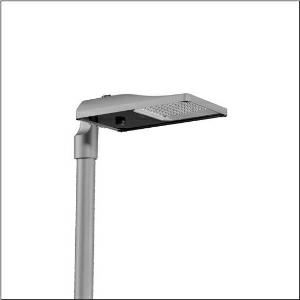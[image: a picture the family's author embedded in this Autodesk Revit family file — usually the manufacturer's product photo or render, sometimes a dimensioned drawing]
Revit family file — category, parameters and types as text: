
# Revit family: streetlight_sl_31_midi___st0_5a_5xh7b31t08ma_78a8
name_source: partatom
category: Lighting Fixtures
units: mm (PartAtom-declared; Revit-internal decimal feet)

## family parameters
Cut with Voids When Loaded = No
Host = Face
Light Source = No
Part Type = Normal
Room Calculation Point = No
Round Connector Dimension = Use Diameter
Shared = No

## types (1)
- --- (1 x LED, 19310 lm, 142.8 W, 3000K)
    Apparent Load = 143 VA
    CIE Flux Codes = 41 75 97 100 100
    Color Rendering = 70
    Color Temperature = 3000K
    Default Elevation = 1800 mm
    Description = Streetlight SL 31 midi D4i, Desk-Remote mast luminaire for post-top, side-entry; light control with lens of PMMA; light distribution: ST0.5a, direct asymmetric distribution, for standard-compliant lighting for roads and squares; LED: luminous flux: 19.310lm, light colour: 730, colour temperature: 3000K; luminous efficacy: 135,2lm/W; control: pre-setting: logarithmic dimming characteristic, flexible luminous flux parameterisation, time-dependent luminous flux control, constant luminous flux control, power reduction, intelligent temperature release in ECG and LED module, overheat protection; luminaire housing, of diecast aluminium, Siteco® metallic grey (DB 702S), corrosivity category C5 high according to DIN EN ISO 12944; cover of toughened safety glass, transparent, opened without tools; mast flange of diecast aluminium, Siteco® metallic grey (DB 702S), spigot size: 76/60mm, mast flange included unmounted; with cable H07RN-F 2x 1.5mm², cable length: 12,5m, connection cable pre-assembled; mains connection: 220..240V, AC, 50/60Hz; power consumption (at start of service life): 142,8W / (at end of service life): 158,8W / (with reduced operation 50%): 60W; protection rating (complete): IP66; insulation class (complete): insulation class II (safety insulation); impact resistance: IK09; certification: CE, ENEC, ENEC+, VDE, UKCA, ZD4i; permissible operating ambient temperature for outdoor applications: -40..+50°C; packaging unit: 1 piece

Light Distribution: ST0.5a
    Height = 79 mm
    Lamp = 1 x LED
    Lamp Light Flux = 19310 lm
    Lamp Power = 142.8 W
    Lamp count = 1
    Length = 577 mm
    Luminous efficacy = 135 lm/W
    Manufacturer = Siteco
    ModVariant = No
    Model = 5XH7B31T08MA
    Number of Poles = 1
    OnlyDefault = Yes
    Power Factor = 1
    Product Name = Streetlight SL 31 midi | ST0.5a
    Product group = mast luminaire | pylon top
    ProductGroupID = 6100
    Protection Class = Protection class II
    Protection Degree = IP 66
    RLX_Detail_Level = 1
    RLX_Emergency_Light_Flux = 0 lm
    RLX_Emergency_Type = 0
    RLX_Emergency_Type_DB = No
    RlxData = <blob elided: 54169 chars, md5=cd5c93c1>
    Socket = socket
    Standby Power = 0 W
    System Light Flux = 19309 lm
    System Power = 143 W
    Type Comments = factory setting: luminous flux: 100 % | dim-lin: 254 | 735 mA
    Type Image = l_1300321.jpg
    URL = http://relux.com
    VarID = @adj_078071
    Voltage = 0 V
    Weight = 0.00 kg
    Width = 362 mm

## geometry (parser evidence)
native form markers: Blend x4, Sweep x11
no freeform markers — native parametric forms only
